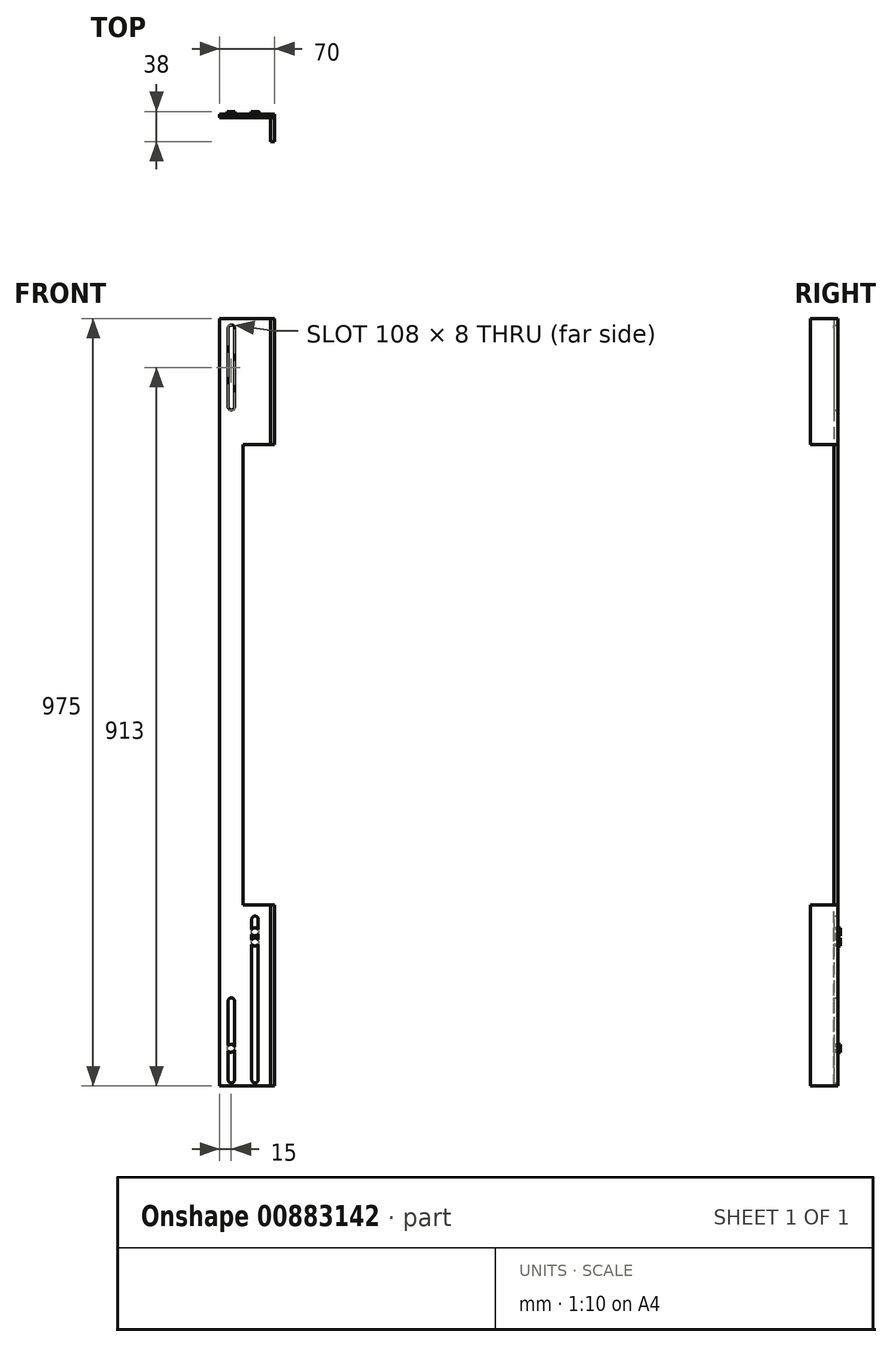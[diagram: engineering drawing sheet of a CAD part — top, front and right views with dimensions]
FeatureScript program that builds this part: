
annotation { "Feature Type Name" : "Feature", "Feature Type Description" : "" }
export const myFeature = defineFeature(function(context is Context, id is Id, definition is map)
    precondition{}
    {
        {
            var Q0;
            Q0=qCreatedBy(makeId("Front.planeOp"),FACE);
            var sketch = newSketch(context, id + "F0", { "sketchPlane" : qUnion([Q0])});
            skLineSegment(sketch, "E0.bottom", {"start": v(0, 0) * mm, "end": v(-70, 0) * mm});
            skLineSegment(sketch, "E0.top", {"start": v(0, 975) * mm, "end": v(-70, 975) * mm});
            skLineSegment(sketch, "E0.left", {"start": v(0, 0) * mm, "end": v(0, 230) * mm});
            skLineSegment(sketch, "E0.right", {"start": v(-70, 0) * mm, "end": v(-70, 975) * mm});
            skLineSegment(sketch, "E1", {"start": v(0, 815) * mm, "end": v(-40, 815) * mm});
            skLineSegment(sketch, "E2", {"start": v(-40, 815) * mm, "end": v(-40, 230) * mm});
            skLineSegment(sketch, "E3", {"start": v(-40, 230) * mm, "end": v(0, 230) * mm});
            skLineSegment(sketch, "E4.trimOffspring", {"start": v(0, 815) * mm, "end": v(0, 975) * mm});
            skArc(sketch, "E5", {"start": v(-51, 108) * mm, "mid": v(-55, 112) * mm, "end": v(-59, 108) * mm});
            skArc(sketch, "E6", {"start": v(-59, 8) * mm, "mid": v(-55, 4) * mm, "end": v(-51, 8) * mm});
            skLineSegment(sketch, "E7", {"start": v(-59, 108) * mm, "end": v(-59, 8) * mm});
            skLineSegment(sketch, "E8", {"start": v(-51, 108) * mm, "end": v(-51, 8) * mm});
            skLineSegment(sketch, "E9", {"start": v(-21.1, 151.4) * mm, "end": v(-21.1, 151.4) * mm});
            skArc(sketch, "E10", {"start": v(-21, 212) * mm, "mid": v(-25, 216) * mm, "end": v(-29, 212) * mm});
            skArc(sketch, "E11", {"start": v(-29, 8) * mm, "mid": v(-25, 4) * mm, "end": v(-21, 8) * mm});
            skLineSegment(sketch, "E12", {"start": v(-29, 212) * mm, "end": v(-29, 8) * mm});
            skLineSegment(sketch, "E13", {"start": v(-21, 212) * mm, "end": v(-21, 8) * mm});
            skArc(sketch, "E14", {"start": v(-51, 963) * mm, "mid": v(-55, 967) * mm, "end": v(-59, 963) * mm});
            skArc(sketch, "E15", {"start": v(-59, 863) * mm, "mid": v(-55, 859) * mm, "end": v(-51, 863) * mm});
            skLineSegment(sketch, "E16", {"start": v(-51, 963) * mm, "end": v(-51, 863) * mm});
            skLineSegment(sketch, "E17", {"start": v(-59, 963) * mm, "end": v(-59, 863) * mm});
            skSolve(sketch);
        }
        {
            var Q0;
            Q0 = qSketchRegion(id + "F0", true);
            extrude(context, id + "F1", {"entities" : qUnion([Q0]), "depth" : 5 * mm, "offsetDistance" : 25 * mm});
        }
        {
            var Q0;
            Q0=makeQuery(id+"F1.opExtrude","CAP_FACE",FACE,{"disambiguationData":[OSD([sQuery(id+"F0.wireOp",EDGE,"E0.bottom"),sQuery(id+"F0.wireOp",EDGE,"E0.top"),sQuery(id+"F0.wireOp",EDGE,"E0.left"),sQuery(id+"F0.wireOp",EDGE,"E0.right"),sQuery(id+"F0.wireOp",EDGE,"E1"),sQuery(id+"F0.wireOp",EDGE,"E2"),sQuery(id+"F0.wireOp",EDGE,"E3"),sQuery(id+"F0.wireOp",EDGE,"E4.trimOffspring"),sQuery(id+"F0.wireOp",EDGE,"E5"),sQuery(id+"F0.wireOp",EDGE,"E6"),sQuery(id+"F0.wireOp",EDGE,"E7"),sQuery(id+"F0.wireOp",EDGE,"E8"),sQuery(id+"F0.wireOp",EDGE,"E10"),sQuery(id+"F0.wireOp",EDGE,"E11"),sQuery(id+"F0.wireOp",EDGE,"E12"),sQuery(id+"F0.wireOp",EDGE,"E13"),sQuery(id+"F0.wireOp",EDGE,"E14"),sQuery(id+"F0.wireOp",EDGE,"E15"),sQuery(id+"F0.wireOp",EDGE,"E16"),sQuery(id+"F0.wireOp",EDGE,"E17")])],"isStart":true});
            cPlane(context, id + "F2", {"entities" : qUnion([Q0]), "cplaneType" : CPlaneType.OFFSET, "offset" : 0 * mm, "width" : 150 * mm, "height" : 150 * mm});
        }
        {
            var Q0;
            Q0=qCreatedBy(id+"F2.planeOp",FACE);
            var sketch = newSketch(context, id + "F3", { "sketchPlane" : qUnion([Q0])});
            skLineSegment(sketch, "E18.top", {"start": v(0, 0) * mm, "end": v(5, 0) * mm});
            skLineSegment(sketch, "E18.left", {"start": v(0, 229.94) * mm, "end": v(0, 0) * mm});
            skLineSegment(sketch, "E18.right", {"start": v(5, 229.94) * mm, "end": v(5, 0) * mm});
            skLineSegment(sketch, "E19", {"start": v(0, 974.95) * mm, "end": v(0, 814.95) * mm});
            skLineSegment(sketch, "E20", {"start": v(0, 814.95) * mm, "end": v(5, 814.95) * mm});
            skLineSegment(sketch, "E21", {"start": v(5, 814.95) * mm, "end": v(5, 974.95) * mm});
            skPoint(sketch, "E22.end.orphan", {"position": v(0, 909.7) * mm});
            skLineSegment(sketch, "E23", {"start": v(5, 974.95) * mm, "end": v(0, 974.95) * mm});
            skPoint(sketch, "E18.bottom.start.orphan", {"position": v(0, 160) * mm});
            skLineSegment(sketch, "E24", {"start": v(5, 229.94) * mm, "end": v(0, 229.94) * mm});
            skSolve(sketch);
        }
        {
            var Q0;
            Q0=makeQuery(id+"F3.imprint","IMPRINT",FACE,{"disambiguationData":[TD([[makeQuery(id+"F3.imprint","IMPRINT",EDGE,{"derivedFrom":sQuery(id+"F3.wireOp",EDGE,"E18.top")}),1.0]])]});
            var Q1;
            Q1=makeQuery(id+"F3.imprint","IMPRINT",FACE,{"disambiguationData":[TD([[makeQuery(id+"F3.imprint","IMPRINT",EDGE,{"derivedFrom":sQuery(id+"F3.wireOp",EDGE,"E19")}),1.0]])]});
            extrude(context, id + "F4", {"entities" : qUnion([Q0, Q1]), "operationType" : NewBodyOperationType.ADD, "oppositeDirection" : true, "depth" : 35 * mm, "offsetDistance" : 25 * mm});
        }
        {
            var Q0;
            Q0=makeQuery(id+"F1.opExtrude","CAP_FACE",FACE,{"disambiguationData":[OSD([sQuery(id+"F0.wireOp",EDGE,"E0.bottom"),sQuery(id+"F0.wireOp",EDGE,"E0.top"),sQuery(id+"F0.wireOp",EDGE,"E0.left"),sQuery(id+"F0.wireOp",EDGE,"E0.right"),sQuery(id+"F0.wireOp",EDGE,"E1"),sQuery(id+"F0.wireOp",EDGE,"E2"),sQuery(id+"F0.wireOp",EDGE,"E3"),sQuery(id+"F0.wireOp",EDGE,"E4.trimOffspring"),sQuery(id+"F0.wireOp",EDGE,"E5"),sQuery(id+"F0.wireOp",EDGE,"E6"),sQuery(id+"F0.wireOp",EDGE,"E7"),sQuery(id+"F0.wireOp",EDGE,"E8"),sQuery(id+"F0.wireOp",EDGE,"E10"),sQuery(id+"F0.wireOp",EDGE,"E11"),sQuery(id+"F0.wireOp",EDGE,"E12"),sQuery(id+"F0.wireOp",EDGE,"E13"),sQuery(id+"F0.wireOp",EDGE,"E14"),sQuery(id+"F0.wireOp",EDGE,"E15"),sQuery(id+"F0.wireOp",EDGE,"E16"),sQuery(id+"F0.wireOp",EDGE,"E17")])],"isStart":false});
            cPlane(context, id + "F5", {"entities" : qUnion([Q0]), "cplaneType" : CPlaneType.OFFSET, "offset" : 0 * mm, "width" : 150 * mm, "height" : 150 * mm});
        }
        {
            var Q0;
            Q0=qCreatedBy(id+"F5.planeOp",FACE);
            var sketch = newSketch(context, id + "F6", { "sketchPlane" : qUnion([Q0])});
            skCircle(sketch, "E25", {"center": v(-25.02, 196) * mm, "radius": 5 * mm});
            skCircle(sketch, "E26", {"center": v(-24.92, 183) * mm, "radius": 5 * mm});
            skCircle(sketch, "E27", {"center": v(-55.55, 48) * mm, "radius": 5 * mm});
            skSolve(sketch);
        }
        {
            var Q0;
            Q0=makeQuery(id+"F6.imprint","IMPRINT",FACE,{"disambiguationData":[TD([[makeQuery(id+"F6.imprint","IMPRINT",EDGE,{"derivedFrom":sQuery(id+"F6.wireOp",EDGE,"E27")}),1.0]])]});
            var Q1;
            Q1=makeQuery(id+"F6.imprint","IMPRINT",FACE,{"disambiguationData":[TD([[makeQuery(id+"F6.imprint","IMPRINT",EDGE,{"derivedFrom":sQuery(id+"F6.wireOp",EDGE,"E26")}),1.0]])]});
            var Q2;
            Q2=makeQuery(id+"F6.imprint","IMPRINT",FACE,{"disambiguationData":[TD([[makeQuery(id+"F6.imprint","IMPRINT",EDGE,{"derivedFrom":sQuery(id+"F6.wireOp",EDGE,"E25")}),1.0]])]});
            extrude(context, id + "F7", {"entities" : qUnion([Q0, Q1, Q2]), "operationType" : NewBodyOperationType.ADD, "oppositeDirection" : true, "depth" : 8 * mm, "offsetDistance" : 25 * mm});
        }
    });
